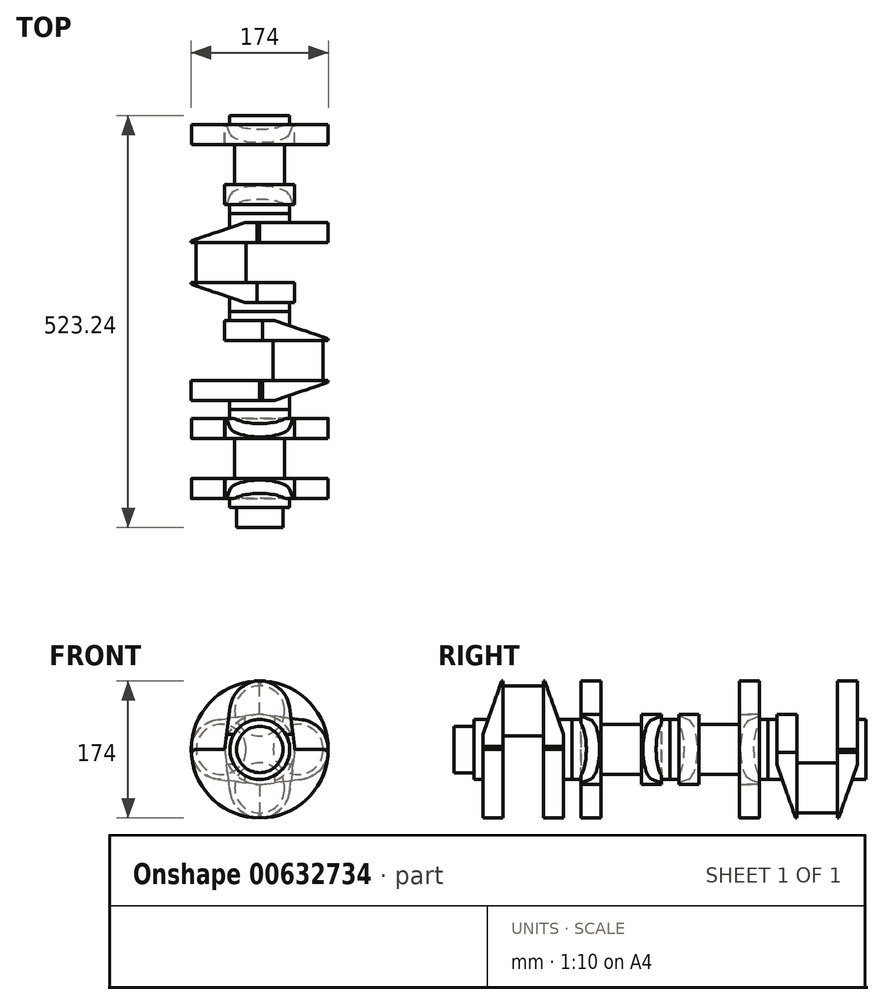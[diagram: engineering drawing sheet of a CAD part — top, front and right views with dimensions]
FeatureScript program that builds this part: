
annotation { "Feature Type Name" : "Feature", "Feature Type Description" : "" }
export const myFeature = defineFeature(function(context is Context, id is Id, definition is map)
    precondition{}
    {
        {
            var Q0;
            Q0=qCreatedBy(makeId("Front.planeOp"),FACE);
            var sketch = newSketch(context, id + "F0", { "sketchPlane" : qUnion([Q0])});
            skArc(sketch, "E0.0", {"start": v(-44.3, 3.62) * mm, "mid": v(0, -44.45) * mm, "end": v(44.3, 3.62) * mm});
            skLineSegment(sketch, "E1", {"start": v(-44.3, 3.62) * mm, "end": v(-37.78, 53.8) * mm});
            skLineSegment(sketch, "E2.MirrorCS", {"start": v(44.3, 3.62) * mm, "end": v(37.78, 53.8) * mm});
            skArc(sketch, "E3.trimOffspring", {"start": v(37.78, 53.8) * mm, "mid": v(0, 87) * mm, "end": v(-37.78, 53.8) * mm});
            skSolve(sketch);
        }
        {
            var Q0;
            Q0=makeQuery(id+"F0.imprint","IMPRINT",FACE,{"disambiguationData":[TD([[makeQuery(id+"F0.imprint","IMPRINT",EDGE,{"derivedFrom":sQuery(id+"F0.wireOp",EDGE,"E0.0")}),1.0]])]});
            extrude(context, id + "F1", {"entities" : qUnion([Q0]), "depth" : 25.4 * mm, "offsetDistance" : 25.4 * mm});
        }
        {
            var Q0;
            Q0=makeQuery(id+"F1.opExtrude","CAP_FACE",FACE,{"disambiguationData":[OSD([sQuery(id+"F0.wireOp",EDGE,"E0.0"),sQuery(id+"F0.wireOp",EDGE,"E1"),sQuery(id+"F0.wireOp",EDGE,"E2.MirrorCS"),sQuery(id+"F0.wireOp",EDGE,"E3.trimOffspring")])],"isStart":false});
            var sketch = newSketch(context, id + "F2", { "sketchPlane" : qUnion([Q0])});
            skCircle(sketch, "E4", {"center": v(0, 48.9) * mm, "radius": 31.75 * mm});
            skSolve(sketch);
        }
        {
            var Q0;
            Q0=makeQuery(id+"F2.imprint","IMPRINT",FACE,{"disambiguationData":[TD([[makeQuery(id+"F2.imprint","IMPRINT",EDGE,{"derivedFrom":sQuery(id+"F2.wireOp",EDGE,"E4")}),1.0]])]});
            extrude(context, id + "F3", {"entities" : qUnion([Q0]), "operationType" : NewBodyOperationType.ADD, "depth" : 25.53 * mm, "offsetDistance" : 25.4 * mm});
        }
        {
            var Q0;
            Q0=makeQuery(id+"F1.opExtrude","CAP_FACE",FACE,{"disambiguationData":[OSD([sQuery(id+"F0.wireOp",EDGE,"E0.0"),sQuery(id+"F0.wireOp",EDGE,"E1"),sQuery(id+"F0.wireOp",EDGE,"E2.MirrorCS"),sQuery(id+"F0.wireOp",EDGE,"E3.trimOffspring")])],"isStart":true});
            var sketch = newSketch(context, id + "F4", { "sketchPlane" : qUnion([Q0])});
            skCircle(sketch, "E5", {"center": v(0, 0) * mm, "radius": 38.1 * mm});
            skSolve(sketch);
        }
        {
            var Q0;
            Q0=makeQuery(id+"F4.imprint","IMPRINT",FACE,{"disambiguationData":[TD([[makeQuery(id+"F4.imprint","IMPRINT",EDGE,{"derivedFrom":sQuery(id+"F4.wireOp",EDGE,"E5")}),1.0]])]});
            extrude(context, id + "F5", {"entities" : qUnion([Q0]), "operationType" : NewBodyOperationType.ADD, "depth" : 11.3 * mm, "offsetDistance" : 25.4 * mm});
        }
        {
            var Q0;
            Q0=makeQuery(id+"F1.opExtrude","CAP_FACE",FACE,{"disambiguationData":[OSD([sQuery(id+"F0.wireOp",EDGE,"E0.0"),sQuery(id+"F0.wireOp",EDGE,"E1"),sQuery(id+"F0.wireOp",EDGE,"E2.MirrorCS"),sQuery(id+"F0.wireOp",EDGE,"E3.trimOffspring")])],"isStart":true});
            var sketch = newSketch(context, id + "F6", { "sketchPlane" : qUnion([Q0])});
            skLineSegment(sketch, "E6", {"start": v(-33.03, 19) * mm, "end": v(-79.58, 19) * mm});
            skLineSegment(sketch, "E7", {"start": v(-79.58, 19) * mm, "end": v(-102.68, 140.56) * mm});
            skLineSegment(sketch, "E8", {"start": v(-102.68, 140.56) * mm, "end": v(107.61, 147.67) * mm});
            skLineSegment(sketch, "E9", {"start": v(107.61, 147.67) * mm, "end": v(137.83, 19) * mm});
            skLineSegment(sketch, "E10", {"start": v(137.83, 19) * mm, "end": v(42.3, 19) * mm});
            skLineSegment(sketch, "E11", {"start": v(42.3, 19) * mm, "end": v(33.03, 19) * mm});
            skSolve(sketch);
        }
        {
            var Q0;
            {var subQ1=sQuery(id+"F6.wireOp",EDGE,"E11");Q0=makeQuery(id+"F6.imprint","IMPRINT",FACE,{"disambiguationData":[TD([[makeQuery(id+"F6.imprint","IMPRINT",EDGE,{"derivedFrom":subQ1}),-1.0]])]});}
            var Q1;
            {var subQ0=sQuery(id+"F6.wireOp",EDGE,"E7");Q1=makeQuery(id+"F6.imprint","IMPRINT",FACE,{"disambiguationData":[TD([[makeQuery(id+"F6.imprint","IMPRINT",EDGE,{"derivedFrom":subQ0}),-1.0]])]});}
            var Q2;
            Q2=sQuery(id+"F6.wireOp",EDGE,"E10");
            revolve(context, id + "F7", {"operationType" : NewBodyOperationType.REMOVE, "entities" : qUnion([Q0, Q1]), "axis" : qUnion([Q2]), "revolveType" : RevolveType.ONE_DIRECTION, "angle" : 19 * degree});
        }
        {
            var Q0;
            Q0=makeQuery(id+"F5.opExtrude","CAP_FACE",FACE,{"disambiguationData":[OSD([sQuery(id+"F4.wireOp",EDGE,"E5")])],"isStart":false});
            extrude(context, id + "F8", {"entities" : qUnion([Q0]), "operationType" : NewBodyOperationType.ADD, "oppositeDirection" : true, "depth" : 32 * mm, "offsetDistance" : 25.4 * mm});
        }
        {
            var Q0;
            Q0=makeQuery(id+"F1.opExtrude","SWEPT_BODY",BODY,{"disambiguationData":[OSD([sQuery(id+"F0.wireOp",EDGE,"E0.0"),sQuery(id+"F0.wireOp",EDGE,"E1"),sQuery(id+"F0.wireOp",EDGE,"E2.MirrorCS"),sQuery(id+"F0.wireOp",EDGE,"E3.trimOffspring")])]});
            var Q1;
            Q1=makeQuery(id+"F3.opExtrude","CAP_FACE",FACE,{"disambiguationData":[OSD([sQuery(id+"F2.wireOp",EDGE,"E4")])],"isStart":false});
            mirror(context, id + "F9", {"operationType" : NewBodyOperationType.ADD, "entities" : qUnion([Q0]), "mirrorPlane" : qUnion([Q1])});
        }
        {
            var Q0;
            Q0=makeQuery(id+"F1.opExtrude","SWEPT_BODY",BODY,{"disambiguationData":[OSD([sQuery(id+"F0.wireOp",EDGE,"E0.0"),sQuery(id+"F0.wireOp",EDGE,"E1"),sQuery(id+"F0.wireOp",EDGE,"E2.MirrorCS"),sQuery(id+"F0.wireOp",EDGE,"E3.trimOffspring")])]});
            var Q1;
            Q1=makeQuery(id+"F5.opExtrude","CAP_FACE",FACE,{"disambiguationData":[OSD([sQuery(id+"F4.wireOp",EDGE,"E5")])],"isStart":false});
            mirror(context, id + "F10", {"entities" : qUnion([Q0]), "mirrorPlane" : qUnion([Q1])});
        }
        {
            var Q0;
            Q0=makeQuery(id+"F10.opPattern","COPY",BODY,{"derivedFrom":makeQuery(id+"F1.opExtrude","SWEPT_BODY",BODY,{"disambiguationData":[OSD([sQuery(id+"F0.wireOp",EDGE,"E0.0"),sQuery(id+"F0.wireOp",EDGE,"E1"),sQuery(id+"F0.wireOp",EDGE,"E2.MirrorCS"),sQuery(id+"F0.wireOp",EDGE,"E3.trimOffspring")])]}),"instanceName":"1"});
            var Q1;
            Q1=makeQuery(id+"F10.opPattern","COPY",FACE,{"derivedFrom":makeQuery(id+"F9.opPattern","COPY",FACE,{"derivedFrom":makeQuery(id+"F5.opExtrude","CAP_FACE",FACE,{"disambiguationData":[OSD([sQuery(id+"F4.wireOp",EDGE,"E5")])],"isStart":false}),"instanceName":"1"}),"instanceName":"1"});
            mirror(context, id + "F11", {"entities" : qUnion([Q0]), "mirrorPlane" : qUnion([Q1])});
        }
        {
            var Q0;
            Q0=makeQuery(id+"F11.opPattern","COPY",BODY,{"derivedFrom":makeQuery(id+"F10.opPattern","COPY",BODY,{"derivedFrom":makeQuery(id+"F1.opExtrude","SWEPT_BODY",BODY,{"disambiguationData":[OSD([sQuery(id+"F0.wireOp",EDGE,"E0.0"),sQuery(id+"F0.wireOp",EDGE,"E1"),sQuery(id+"F0.wireOp",EDGE,"E2.MirrorCS"),sQuery(id+"F0.wireOp",EDGE,"E3.trimOffspring")])]}),"instanceName":"1"}),"instanceName":"1"});
            var Q1;
            Q1=makeQuery(id+"F11.opPattern","COPY",FACE,{"derivedFrom":makeQuery(id+"F10.opPattern","COPY",FACE,{"derivedFrom":makeQuery(id+"F5.opExtrude","CAP_FACE",FACE,{"disambiguationData":[OSD([sQuery(id+"F4.wireOp",EDGE,"E5")])],"isStart":false}),"instanceName":"1"}),"instanceName":"1"});
            mirror(context, id + "F12", {"entities" : qUnion([Q0]), "mirrorPlane" : qUnion([Q1])});
        }
        {
            var Q0;
            Q0=makeQuery(id+"F10.opPattern","COPY",BODY,{"derivedFrom":makeQuery(id+"F1.opExtrude","SWEPT_BODY",BODY,{"disambiguationData":[OSD([sQuery(id+"F0.wireOp",EDGE,"E0.0"),sQuery(id+"F0.wireOp",EDGE,"E1"),sQuery(id+"F0.wireOp",EDGE,"E2.MirrorCS"),sQuery(id+"F0.wireOp",EDGE,"E3.trimOffspring")])]}),"instanceName":"1"});
            var Q1;
            Q1=makeQuery(id+"F9.opPattern","COPY",FACE,{"derivedFrom":makeQuery(id+"F5.opExtrude","SWEPT_FACE",FACE,{"disambiguationData":[OSD([sQuery(id+"F4.wireOp",EDGE,"E5")])]}),"instanceName":"1"});
            transform(context, id + "F13", {"entities" : qUnion([Q0]), "transformType" : TransformType.ROTATION, "transformAxis" : qUnion([Q1]), "angle" : 90 * degree, "makeCopy" : false});
        }
        {
            var Q0;
            Q0=makeQuery(id+"F11.opPattern","COPY",BODY,{"derivedFrom":makeQuery(id+"F10.opPattern","COPY",BODY,{"derivedFrom":makeQuery(id+"F1.opExtrude","SWEPT_BODY",BODY,{"disambiguationData":[OSD([sQuery(id+"F0.wireOp",EDGE,"E0.0"),sQuery(id+"F0.wireOp",EDGE,"E1"),sQuery(id+"F0.wireOp",EDGE,"E2.MirrorCS"),sQuery(id+"F0.wireOp",EDGE,"E3.trimOffspring")])]}),"instanceName":"1"}),"instanceName":"1"});
            var Q1;
            Q1=makeQuery(id+"F9.opPattern","COPY",FACE,{"derivedFrom":makeQuery(id+"F5.opExtrude","SWEPT_FACE",FACE,{"disambiguationData":[OSD([sQuery(id+"F4.wireOp",EDGE,"E5")])]}),"instanceName":"1"});
            transform(context, id + "F14", {"entities" : qUnion([Q0]), "transformType" : TransformType.ROTATION, "transformAxis" : qUnion([Q1]), "angle" : 90 * degree, "oppositeDirection" : true, "makeCopy" : false});
        }
        {
            var Q0;
            Q0=makeQuery(id+"F12.opPattern","COPY",BODY,{"derivedFrom":makeQuery(id+"F11.opPattern","COPY",BODY,{"derivedFrom":makeQuery(id+"F10.opPattern","COPY",BODY,{"derivedFrom":makeQuery(id+"F1.opExtrude","SWEPT_BODY",BODY,{"disambiguationData":[OSD([sQuery(id+"F0.wireOp",EDGE,"E0.0"),sQuery(id+"F0.wireOp",EDGE,"E1"),sQuery(id+"F0.wireOp",EDGE,"E2.MirrorCS"),sQuery(id+"F0.wireOp",EDGE,"E3.trimOffspring")])]}),"instanceName":"1"}),"instanceName":"1"}),"instanceName":"1"});
            var Q1;
            Q1=makeQuery(id+"F9.opPattern","COPY",FACE,{"derivedFrom":makeQuery(id+"F5.opExtrude","SWEPT_FACE",FACE,{"disambiguationData":[OSD([sQuery(id+"F4.wireOp",EDGE,"E5")])]}),"instanceName":"1"});
            transform(context, id + "F15", {"entities" : qUnion([Q0]), "transformType" : TransformType.ROTATION, "transformAxis" : qUnion([Q1]), "angle" : 180 * degree, "makeCopy" : false});
        }
        {
            var Q0;
            Q0=makeQuery(id+"F9.opPattern","COPY",FACE,{"derivedFrom":makeQuery(id+"F1.opExtrude","CAP_FACE",FACE,{"disambiguationData":[OSD([sQuery(id+"F0.wireOp",EDGE,"E0.0"),sQuery(id+"F0.wireOp",EDGE,"E1"),sQuery(id+"F0.wireOp",EDGE,"E2.MirrorCS"),sQuery(id+"F0.wireOp",EDGE,"E3.trimOffspring")])],"isStart":true}),"instanceName":"1"});
            var sketch = newSketch(context, id + "F16", { "sketchPlane" : qUnion([Q0])});
            skArc(sketch, "E12", {"start": v(-86.72, -6.85) * mm, "mid": v(0, -87) * mm, "end": v(86.72, -6.85) * mm});
            skLineSegment(sketch, "E13", {"start": v(-44.45, 0) * mm, "end": v(-80.4, 0) * mm});
            skLineSegment(sketch, "E14", {"start": v(44.45, 0) * mm, "end": v(80.4, 0) * mm});
            skPoint(sketch, "E15.visualSharp", {"position": v(-87, 0) * mm});
            skArc(sketch, "E15.filletArc", {"start": v(-80.4, 0) * mm, "mid": v(-85.06, -2.04) * mm, "end": v(-86.72, -6.85) * mm});
            skPoint(sketch, "E16.visualSharp", {"position": v(87, 0) * mm});
            skArc(sketch, "E16.filletArc", {"start": v(86.72, -6.85) * mm, "mid": v(85.06, -2.04) * mm, "end": v(80.4, 0) * mm});
            skSolve(sketch);
        }
        {
            var Q0;
            Q0=makeQuery(id+"F16.imprint","IMPRINT",FACE,{"disambiguationData":[TD([[makeQuery(id+"F16.imprint","IMPRINT",EDGE,{"derivedFrom":sQuery(id+"F16.wireOp",EDGE,"E12")}),1.0]])]});
            var Q1;
            Q1=makeQuery(id+"F9.opPattern","COPY",FACE,{"derivedFrom":makeQuery(id+"F1.opExtrude","CAP_FACE",FACE,{"disambiguationData":[OSD([sQuery(id+"F0.wireOp",EDGE,"E0.0"),sQuery(id+"F0.wireOp",EDGE,"E1"),sQuery(id+"F0.wireOp",EDGE,"E2.MirrorCS"),sQuery(id+"F0.wireOp",EDGE,"E3.trimOffspring")])],"isStart":false}),"instanceName":"1"});
            extrude(context, id + "F17", {"entities" : qUnion([Q0]), "operationType" : NewBodyOperationType.ADD, "endBound" : BoundingType.UP_TO_SURFACE, "oppositeDirection" : true, "depth" : 25.4 * mm, "endBoundEntityFace" : qUnion([Q1]), "offsetDistance" : 25.4 * mm});
        }
        {
            var Q0;
            Q0=makeQuery(id+"F1.opExtrude","CAP_FACE",FACE,{"disambiguationData":[OSD([sQuery(id+"F0.wireOp",EDGE,"E0.0"),sQuery(id+"F0.wireOp",EDGE,"E1"),sQuery(id+"F0.wireOp",EDGE,"E2.MirrorCS"),sQuery(id+"F0.wireOp",EDGE,"E3.trimOffspring")])],"isStart":false});
            var sketch = newSketch(context, id + "F18", { "sketchPlane" : qUnion([Q0])});
            skArc(sketch, "E17.0", {"start": v(-86.72, -6.85) * mm, "mid": v(0, -87) * mm, "end": v(86.72, -6.85) * mm});
            skLineSegment(sketch, "E18.0", {"start": v(-44.45, 0) * mm, "end": v(-80.4, 0) * mm});
            skArc(sketch, "E19.0", {"start": v(-80.4, 0) * mm, "mid": v(-85.06, -2.04) * mm, "end": v(-86.72, -6.85) * mm});
            skLineSegment(sketch, "E20.0", {"start": v(44.45, 0) * mm, "end": v(80.4, 0) * mm});
            skArc(sketch, "E21.0", {"start": v(86.72, -6.85) * mm, "mid": v(85.06, -2.04) * mm, "end": v(80.4, 0) * mm});
            skSolve(sketch);
        }
        {
            var Q0;
            Q0=makeQuery(id+"F18.imprint","IMPRINT",FACE,{"disambiguationData":[TD([[makeQuery(id+"F18.imprint","IMPRINT",EDGE,{"derivedFrom":sQuery(id+"F18.wireOp",EDGE,"E17.0")}),1.0]])]});
            var Q1;
            Q1=makeQuery(id+"F1.opExtrude","CAP_FACE",FACE,{"disambiguationData":[OSD([sQuery(id+"F0.wireOp",EDGE,"E0.0"),sQuery(id+"F0.wireOp",EDGE,"E1"),sQuery(id+"F0.wireOp",EDGE,"E2.MirrorCS"),sQuery(id+"F0.wireOp",EDGE,"E3.trimOffspring")])],"isStart":true});
            extrude(context, id + "F19", {"entities" : qUnion([Q0]), "operationType" : NewBodyOperationType.ADD, "endBound" : BoundingType.UP_TO_SURFACE, "oppositeDirection" : true, "depth" : 25.4 * mm, "endBoundEntityFace" : qUnion([Q1]), "offsetDistance" : 25.4 * mm});
        }
        {
            var Q0;
            Q0=makeQuery(id+"F10.opPattern","COPY",FACE,{"derivedFrom":makeQuery(id+"F1.opExtrude","CAP_FACE",FACE,{"disambiguationData":[OSD([sQuery(id+"F0.wireOp",EDGE,"E0.0"),sQuery(id+"F0.wireOp",EDGE,"E1"),sQuery(id+"F0.wireOp",EDGE,"E2.MirrorCS"),sQuery(id+"F0.wireOp",EDGE,"E3.trimOffspring")])],"isStart":true}),"instanceName":"1"});
            var sketch = newSketch(context, id + "F20", { "sketchPlane" : qUnion([Q0])});
            skArc(sketch, "E22", {"start": v(-6.85, 86.72) * mm, "mid": v(-87, 0) * mm, "end": v(-6.85, -86.72) * mm});
            skLineSegment(sketch, "E23", {"start": v(0, 44.3) * mm, "end": v(0, 80.4) * mm});
            skLineSegment(sketch, "E24", {"start": v(0, -44.45) * mm, "end": v(0, -80.4) * mm});
            skPoint(sketch, "E25.visualSharp", {"position": v(0, -87) * mm});
            skArc(sketch, "E25.filletArc", {"start": v(-6.85, -86.72) * mm, "mid": v(-2.04, -85.06) * mm, "end": v(0, -80.4) * mm});
            skPoint(sketch, "E26.visualSharp", {"position": v(0, 87) * mm});
            skArc(sketch, "E26.filletArc", {"start": v(0, 80.4) * mm, "mid": v(-2.04, 85.06) * mm, "end": v(-6.85, 86.72) * mm});
            skSolve(sketch);
        }
        {
            var Q0;
            Q0=makeQuery(id+"F20.imprint","IMPRINT",FACE,{"disambiguationData":[TD([[makeQuery(id+"F20.imprint","IMPRINT",EDGE,{"derivedFrom":sQuery(id+"F20.wireOp",EDGE,"E22")}),1.0]])]});
            var Q1;
            Q1=makeQuery(id+"F10.opPattern","COPY",FACE,{"derivedFrom":makeQuery(id+"F1.opExtrude","CAP_FACE",FACE,{"disambiguationData":[OSD([sQuery(id+"F0.wireOp",EDGE,"E0.0"),sQuery(id+"F0.wireOp",EDGE,"E1"),sQuery(id+"F0.wireOp",EDGE,"E2.MirrorCS"),sQuery(id+"F0.wireOp",EDGE,"E3.trimOffspring")])],"isStart":false}),"instanceName":"1"});
            extrude(context, id + "F21", {"entities" : qUnion([Q0]), "operationType" : NewBodyOperationType.ADD, "endBound" : BoundingType.UP_TO_SURFACE, "oppositeDirection" : true, "depth" : 25.4 * mm, "endBoundEntityFace" : qUnion([Q1]), "offsetDistance" : 25.4 * mm});
        }
        {
            var Q0;
            Q0=makeQuery(id+"F11.opPattern","COPY",FACE,{"derivedFrom":makeQuery(id+"F10.opPattern","COPY",FACE,{"derivedFrom":makeQuery(id+"F1.opExtrude","CAP_FACE",FACE,{"disambiguationData":[OSD([sQuery(id+"F0.wireOp",EDGE,"E0.0"),sQuery(id+"F0.wireOp",EDGE,"E1"),sQuery(id+"F0.wireOp",EDGE,"E2.MirrorCS"),sQuery(id+"F0.wireOp",EDGE,"E3.trimOffspring")])],"isStart":false}),"instanceName":"1"}),"instanceName":"1"});
            var sketch = newSketch(context, id + "F22", { "sketchPlane" : qUnion([Q0])});
            skArc(sketch, "E27", {"start": v(6.85, -86.72) * mm, "mid": v(87, 0) * mm, "end": v(6.85, 86.72) * mm});
            skLineSegment(sketch, "E28", {"start": v(0, 44.45) * mm, "end": v(0, 80.4) * mm});
            skLineSegment(sketch, "E29", {"start": v(0, -44.45) * mm, "end": v(0, -80.4) * mm});
            skPoint(sketch, "E30.visualSharp", {"position": v(0, 87) * mm});
            skArc(sketch, "E30.filletArc", {"start": v(6.85, 86.72) * mm, "mid": v(2.04, 85.06) * mm, "end": v(0, 80.4) * mm});
            skPoint(sketch, "E31.visualSharp", {"position": v(0, -87) * mm});
            skArc(sketch, "E31.filletArc", {"start": v(0, -80.4) * mm, "mid": v(2.04, -85.06) * mm, "end": v(6.85, -86.72) * mm});
            skSolve(sketch);
        }
        {
            var Q0;
            Q0=makeQuery(id+"F22.imprint","IMPRINT",FACE,{"disambiguationData":[TD([[makeQuery(id+"F22.imprint","IMPRINT",EDGE,{"derivedFrom":sQuery(id+"F22.wireOp",EDGE,"E27")}),1.0]])]});
            var Q1;
            Q1=makeQuery(id+"F11.opPattern","COPY",FACE,{"derivedFrom":makeQuery(id+"F10.opPattern","COPY",FACE,{"derivedFrom":makeQuery(id+"F1.opExtrude","CAP_FACE",FACE,{"disambiguationData":[OSD([sQuery(id+"F0.wireOp",EDGE,"E0.0"),sQuery(id+"F0.wireOp",EDGE,"E1"),sQuery(id+"F0.wireOp",EDGE,"E2.MirrorCS"),sQuery(id+"F0.wireOp",EDGE,"E3.trimOffspring")])],"isStart":true}),"instanceName":"1"}),"instanceName":"1"});
            extrude(context, id + "F23", {"entities" : qUnion([Q0]), "operationType" : NewBodyOperationType.ADD, "endBound" : BoundingType.UP_TO_SURFACE, "oppositeDirection" : true, "depth" : 25.4 * mm, "endBoundEntityFace" : qUnion([Q1]), "offsetDistance" : 25.4 * mm});
        }
        {
            var Q0;
            Q0=makeQuery(id+"F12.opPattern","COPY",FACE,{"derivedFrom":makeQuery(id+"F11.opPattern","COPY",FACE,{"derivedFrom":makeQuery(id+"F10.opPattern","COPY",FACE,{"derivedFrom":makeQuery(id+"F9.opPattern","COPY",FACE,{"derivedFrom":makeQuery(id+"F1.opExtrude","CAP_FACE",FACE,{"disambiguationData":[OSD([sQuery(id+"F0.wireOp",EDGE,"E0.0"),sQuery(id+"F0.wireOp",EDGE,"E1"),sQuery(id+"F0.wireOp",EDGE,"E2.MirrorCS"),sQuery(id+"F0.wireOp",EDGE,"E3.trimOffspring")])],"isStart":true}),"instanceName":"1"}),"instanceName":"1"}),"instanceName":"1"}),"instanceName":"1"});
            var sketch = newSketch(context, id + "F24", { "sketchPlane" : qUnion([Q0])});
            skArc(sketch, "E32", {"start": v(86.72, 6.85) * mm, "mid": v(0, 87) * mm, "end": v(-86.72, 6.85) * mm});
            skLineSegment(sketch, "E33", {"start": v(-44.45, 0) * mm, "end": v(-80.4, 0) * mm});
            skLineSegment(sketch, "E34", {"start": v(44.45, 0) * mm, "end": v(80.4, 0) * mm});
            skPoint(sketch, "E35.visualSharp", {"position": v(-87, 0) * mm});
            skArc(sketch, "E35.filletArc", {"start": v(-86.72, 6.85) * mm, "mid": v(-85.06, 2.04) * mm, "end": v(-80.4, 0) * mm});
            skPoint(sketch, "E36.visualSharp", {"position": v(87, 0) * mm});
            skArc(sketch, "E36.filletArc", {"start": v(80.4, 0) * mm, "mid": v(85.06, 2.04) * mm, "end": v(86.72, 6.85) * mm});
            skSolve(sketch);
        }
        {
            var Q0;
            Q0=makeQuery(id+"F24.imprint","IMPRINT",FACE,{"disambiguationData":[TD([[makeQuery(id+"F24.imprint","IMPRINT",EDGE,{"derivedFrom":sQuery(id+"F24.wireOp",EDGE,"E32")}),1.0]])]});
            var Q1;
            Q1=makeQuery(id+"F12.opPattern","COPY",FACE,{"derivedFrom":makeQuery(id+"F11.opPattern","COPY",FACE,{"derivedFrom":makeQuery(id+"F10.opPattern","COPY",FACE,{"derivedFrom":makeQuery(id+"F9.opPattern","COPY",FACE,{"derivedFrom":makeQuery(id+"F1.opExtrude","CAP_FACE",FACE,{"disambiguationData":[OSD([sQuery(id+"F0.wireOp",EDGE,"E0.0"),sQuery(id+"F0.wireOp",EDGE,"E1"),sQuery(id+"F0.wireOp",EDGE,"E2.MirrorCS"),sQuery(id+"F0.wireOp",EDGE,"E3.trimOffspring")])],"isStart":false}),"instanceName":"1"}),"instanceName":"1"}),"instanceName":"1"}),"instanceName":"1"});
            extrude(context, id + "F25", {"entities" : qUnion([Q0]), "operationType" : NewBodyOperationType.ADD, "endBound" : BoundingType.UP_TO_SURFACE, "oppositeDirection" : true, "depth" : 25.4 * mm, "endBoundEntityFace" : qUnion([Q1]), "offsetDistance" : 25.4 * mm});
        }
        {
            var Q0;
            Q0=makeQuery(id+"F12.opPattern","COPY",FACE,{"derivedFrom":makeQuery(id+"F11.opPattern","COPY",FACE,{"derivedFrom":makeQuery(id+"F10.opPattern","COPY",FACE,{"derivedFrom":makeQuery(id+"F1.opExtrude","CAP_FACE",FACE,{"disambiguationData":[OSD([sQuery(id+"F0.wireOp",EDGE,"E0.0"),sQuery(id+"F0.wireOp",EDGE,"E1"),sQuery(id+"F0.wireOp",EDGE,"E2.MirrorCS"),sQuery(id+"F0.wireOp",EDGE,"E3.trimOffspring")])],"isStart":false}),"instanceName":"1"}),"instanceName":"1"}),"instanceName":"1"});
            var Q1;
            {var subQ0=sQuery(id+"F0.wireOp",EDGE,"E3.trimOffspring");var subQ1=sQuery(id+"F0.wireOp",EDGE,"E2.MirrorCS");var subQ2=sQuery(id+"F0.wireOp",EDGE,"E1");var subQ3=sQuery(id+"F0.wireOp",EDGE,"E0.0");Q1=makeQuery(id+"F25.boolean.opBoolean","MERGE",FACE,{"derivedFrom":[makeQuery(id+"F12.opPattern","COPY",FACE,{"derivedFrom":makeQuery(id+"F11.opPattern","COPY",FACE,{"derivedFrom":makeQuery(id+"F10.opPattern","COPY",FACE,{"derivedFrom":makeQuery(id+"F9.opPattern","COPY",FACE,{"derivedFrom":makeQuery(id+"F1.opExtrude","CAP_FACE",FACE,{"disambiguationData":[OSD([subQ3,subQ2,subQ1,subQ0])],"isStart":false}),"instanceName":"1"}),"instanceName":"1"}),"instanceName":"1"}),"instanceName":"1"}),makeQuery(id+"F25.opExtrude","CAP_FACE",FACE,{"disambiguationData":[OSD([subQ3,subQ2,subQ1,subQ0])],"isStart":false})]});}
            cPlane(context, id + "F26", {"entities" : qUnion([Q0, Q1]), "cplaneType" : CPlaneType.MID_PLANE, "offset" : 25.4 * mm, "width" : 152.4 * mm, "height" : 152.4 * mm});
        }
        {
            var Q0;
            Q0=qCreatedBy(makeId("Right.planeOp"),FACE);
            var sketch = newSketch(context, id + "F27", { "sketchPlane" : qUnion([Q0])});
            skLineSegment(sketch, "E37", {"start": v(347.98, -3.62) * mm, "end": v(347.98, 239.11) * mm});
            skLineSegment(sketch, "E38.MirrorCS", {"start": v(296.93, -3.62) * mm, "end": v(296.93, 239.11) * mm});
            skLineSegment(sketch, "E39", {"start": v(296.93, 239.11) * mm, "end": v(347.98, 239.11) * mm});
            skLineSegment(sketch, "E40", {"start": v(296.93, -3.62) * mm, "end": v(347.98, -3.62) * mm});
            skSolve(sketch);
        }
        {
            var Q0;
            Q0 = qSketchRegion(id + "F27", true);
            extrude(context, id + "F28", {"entities" : qUnion([Q0]), "operationType" : NewBodyOperationType.REMOVE, "endBound" : BoundingType.SYMMETRIC, "oppositeDirection" : true, "depth" : 420.62 * mm, "offsetDistance" : 25.4 * mm});
        }
        {
            var Q0;
            Q0=makeQuery(id+"F9.opPattern","COPY",FACE,{"derivedFrom":makeQuery(id+"F5.opExtrude","CAP_FACE",FACE,{"disambiguationData":[OSD([sQuery(id+"F4.wireOp",EDGE,"E5")])],"isStart":false}),"instanceName":"1"});
            var sketch = newSketch(context, id + "F29", { "sketchPlane" : qUnion([Q0])});
            skCircle(sketch, "E41", {"center": v(0, 0) * mm, "radius": 29.52 * mm});
            skSolve(sketch);
        }
        {
            var Q0;
            Q0=makeQuery(id+"F29.imprint","IMPRINT",FACE,{"disambiguationData":[TD([[makeQuery(id+"F29.imprint","IMPRINT",EDGE,{"derivedFrom":sQuery(id+"F29.wireOp",EDGE,"E41")}),1.0]])]});
            extrude(context, id + "F30", {"entities" : qUnion([Q0]), "operationType" : NewBodyOperationType.ADD, "depth" : 25.4 * mm, "offsetDistance" : 25.4 * mm});
        }
    });
